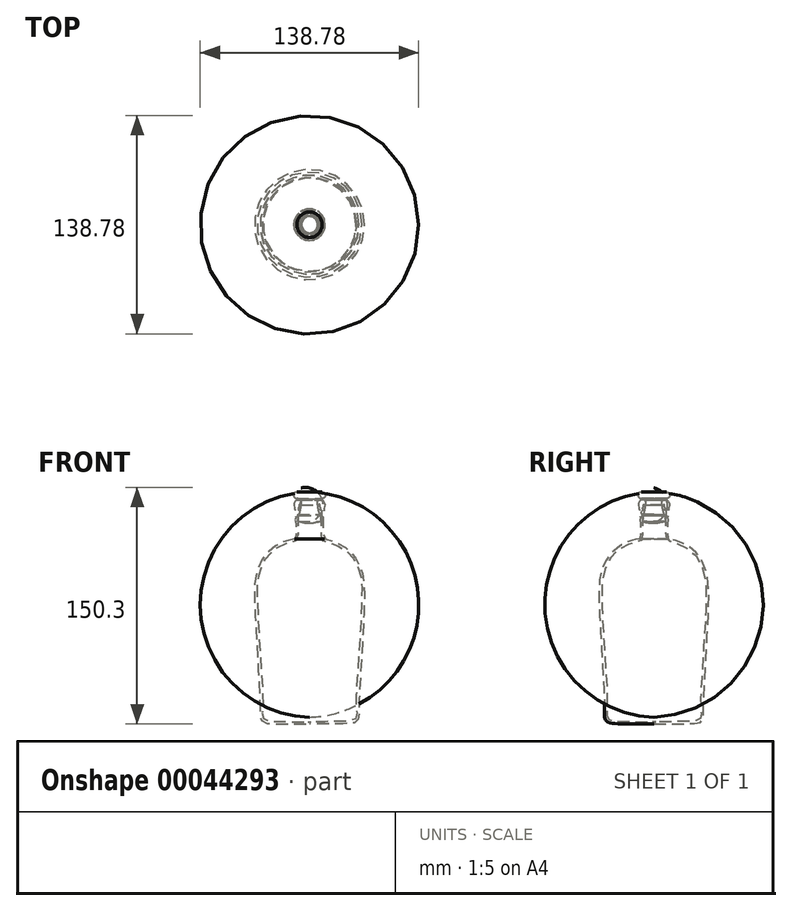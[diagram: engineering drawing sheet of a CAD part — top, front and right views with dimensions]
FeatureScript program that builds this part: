
annotation { "Feature Type Name" : "Feature", "Feature Type Description" : "" }
export const myFeature = defineFeature(function(context is Context, id is Id, definition is map)
    precondition{}
    {
        {
            var Q0;
            Q0=qCreatedBy(makeId("Front.planeOp"),FACE);
            var sketch = newSketch(context, id + "F0", { "sketchPlane" : qUnion([Q0])});
            skFitSpline(sketch, "E0", {"points": [v(16.35, 89.56) * mm, v(17.45, 88.06) * mm, v(17.9, 85.9) * mm, v(17.45, 84.56) * mm, v(17.3, 84.11) * mm, v(17.43, 83.67) * mm, v(17.16, 83.29) * mm, v(17.03, 82.98) * mm, v(17.56, 82.4) * mm, v(17.92, 81.64) * mm, v(17.83, 80.7) * mm, v(17.05, 79.8) * mm, v(16.54, 79.06) * mm, v(17.1, 64.7) * mm, v(17.4, 64.62) * mm, v(22.34, 63.43) * mm, v(30.8, 59.34) * mm, v(41.05, 45.04) * mm, v(42.4, 15.1) * mm, v(40.89, -12.65) * mm, v(39.37, -44.6) * mm, v(39.34, -48.68) * mm, v(38.2, -50.95) * mm, v(37.07, -51.99) * mm, v(28.77, -52.74) * mm, v(7.95, -52.93) * mm], "startDerivative": vector(47.52, -53.56) * mm, "endDerivative": vector(-240.4, -1.4) * mm});
            skArc(sketch, "E1", {"start": v(16.35, 89.56) * mm, "mid": v(15.01, 89.86) * mm, "end": v(13.68, 89.56) * mm});
            skFitSpline(sketch, "E2", {"points": [v(13.68, 89.56) * mm, v(13.68, 88.83) * mm, v(14.03, 87.08) * mm, v(14.73, 86.08) * mm, v(14.68, 84.88) * mm, v(15.18, 84.03) * mm, v(14.88, 83.18) * mm, v(15.83, 82.38) * mm, v(15.58, 80.33) * mm], "startDerivative": vector(-0.15, -6.45) * mm, "endDerivative": vector(-5.38, -14.73) * mm});
            skFitSpline(sketch, "E3", {"points": [v(15.58, 80.33) * mm, v(15.14, 74.09) * mm, v(15.15, 71.15) * mm, v(15.58, 65.02) * mm, v(16.03, 63.63) * mm, v(17.5, 63.31) * mm, v(28.56, 58.96) * mm, v(35.75, 52.44) * mm, v(39.9, 43) * mm, v(41.25, 28.7) * mm, v(38, -27.94) * mm, v(37.65, -41.79) * mm, v(37.88, -47.76) * mm, v(36.2, -50.35) * mm, v(29.35, -51.26) * mm, v(7.95, -51.48) * mm], "startDerivative": vector(-9.99, -128) * mm, "endDerivative": vector(-233.78, 0.39) * mm});
            skLineSegment(sketch, "E4", {"start": v(7.95, -52.93) * mm, "end": v(7.95, -36.69) * mm, "construction": true});
            skLineSegment(sketch, "E5", {"start": v(7.95, -52.93) * mm, "end": v(7.95, -51.48) * mm});
            skSolve(sketch);
        }
        {
            var Q0;
            Q0=qCreatedBy(makeId("Front.planeOp"),FACE);
            var sketch = newSketch(context, id + "F1", { "sketchPlane" : qUnion([Q0])});
            skLineSegment(sketch, "E6.0", {"start": v(7.95, -52.93) * mm, "end": v(7.95, -36.69) * mm, "construction": true});
            skSolve(sketch);
        }
        {
            var Q0;
            Q0 = qSketchRegion(id + "F0", true);
            var Q1;
            Q1=sQuery(id+"F1.wireOp",EDGE,"E6.0");
            revolve(context, id + "F2", {"entities" : qUnion([Q0]), "axis" : qUnion([Q1]), "revolveType" : RevolveType.FULL});
        }
        {
            var Q0;
            Q0=qCreatedBy(makeId("Front.planeOp"),FACE);
            var sketch = newSketch(context, id + "F3", { "sketchPlane" : qUnion([Q0])});
            skLineSegment(sketch, "E7.0", {"start": v(16.35, 89.56) * mm, "end": v(-0.44, 89.56) * mm, "construction": true});
            skLineSegment(sketch, "E8", {"start": v(7.95, 89.56) * mm, "end": v(7.95, 73.95) * mm, "construction": true});
            skPoint(sketch, "E8.endSnap0", {"position": v(7.95, 89.56) * mm});
            skLineSegment(sketch, "E9", {"start": v(7.95, 89.56) * mm, "end": v(7.95, 95.17) * mm, "construction": true});
            skArc(sketch, "E10", {"start": v(16.03, 94.4) * mm, "mid": v(12, 94.6) * mm, "end": v(7.95, 94.6) * mm});
            skArc(sketch, "E11", {"start": v(13.52, 89.56) * mm, "mid": v(13.1, 87.88) * mm, "end": v(13.18, 86.16) * mm});
            skArc(sketch, "E12", {"start": v(13.18, 86.16) * mm, "mid": v(13.75, 82.88) * mm, "end": v(14.58, 79.66) * mm});
            skArc(sketch, "E13", {"start": v(15.08, 75.85) * mm, "mid": v(15.03, 77.78) * mm, "end": v(14.58, 79.66) * mm});
            skArc(sketch, "E14", {"start": v(7.95, 75.22) * mm, "mid": v(11.57, 74.95) * mm, "end": v(15.08, 75.85) * mm});
            skLineSegment(sketch, "E15", {"start": v(7.95, 94.6) * mm, "end": v(7.95, 75.22) * mm});
            skArc(sketch, "E16", {"start": v(15.99, 90.38) * mm, "mid": v(18.02, 92.36) * mm, "end": v(16.03, 94.4) * mm});
            skArc(sketch, "E17", {"start": v(15.99, 90.38) * mm, "mid": v(14.72, 90.07) * mm, "end": v(13.52, 89.56) * mm});
            skSolve(sketch);
        }
        {
            var Q0;
            Q0=makeQuery(id+"F3.imprint","IMPRINT",FACE,{"disambiguationData":[TD([[makeQuery(id+"F3.imprint","IMPRINT",EDGE,{"derivedFrom":sQuery(id+"F3.wireOp",EDGE,"E10")}),1.0]])]});
            var Q1;
            Q1=sQuery(id+"F3.wireOp",EDGE,"E9");
            revolve(context, id + "F4", {"entities" : qUnion([Q0]), "axis" : qUnion([Q1]), "revolveType" : RevolveType.FULL});
        }
    });
